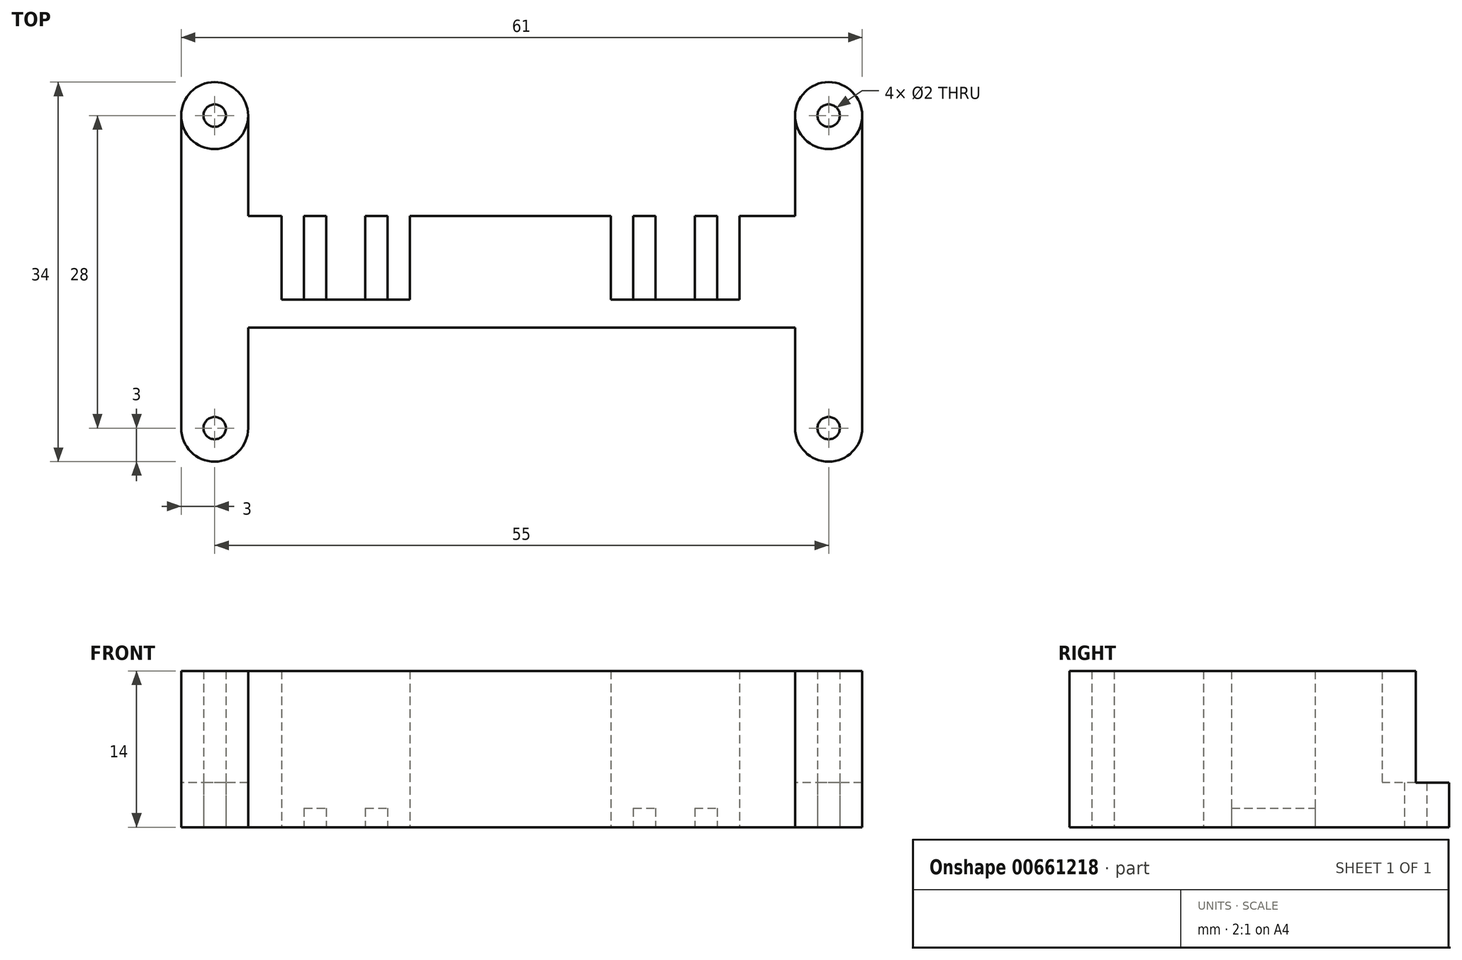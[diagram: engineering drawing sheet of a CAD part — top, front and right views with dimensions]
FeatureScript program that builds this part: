
annotation { "Feature Type Name" : "Feature", "Feature Type Description" : "" }
export const myFeature = defineFeature(function(context is Context, id is Id, definition is map)
    precondition{}
    {
        {
            var Q0;
            Q0=qCreatedBy(makeId("Top.planeOp"),FACE);
            var sketch = newSketch(context, id + "F0", { "sketchPlane" : qUnion([Q0])});
            skLineSegment(sketch, "E0", {"start": v(55, 0) * mm, "end": v(55, -9) * mm});
            skLineSegment(sketch, "E1", {"start": v(61, -9) * mm, "end": v(61, 19) * mm});
            skLineSegment(sketch, "E2", {"start": v(55, 19) * mm, "end": v(55, 10) * mm});
            skLineSegment(sketch, "E3", {"start": v(55, 10) * mm, "end": v(50, 10) * mm});
            skLineSegment(sketch, "E4", {"start": v(50, 10) * mm, "end": v(50, 2.5) * mm});
            skLineSegment(sketch, "E5", {"start": v(50, 2.5) * mm, "end": v(38.5, 2.5) * mm});
            skLineSegment(sketch, "E6", {"start": v(38.5, 2.5) * mm, "end": v(38.5, 10) * mm});
            skLineSegment(sketch, "E7", {"start": v(38.5, 10) * mm, "end": v(20.5, 10) * mm});
            skLineSegment(sketch, "E8", {"start": v(20.5, 10) * mm, "end": v(20.5, 2.5) * mm});
            skLineSegment(sketch, "E9", {"start": v(20.5, 2.5) * mm, "end": v(9, 2.5) * mm});
            skLineSegment(sketch, "E10", {"start": v(9, 2.5) * mm, "end": v(9, 10) * mm});
            skLineSegment(sketch, "E11", {"start": v(9, 10) * mm, "end": v(6, 10) * mm});
            skLineSegment(sketch, "E12", {"start": v(6, 10) * mm, "end": v(6, 19) * mm});
            skLineSegment(sketch, "E13", {"start": v(0, 19) * mm, "end": v(0, -9) * mm});
            skLineSegment(sketch, "E14", {"start": v(6, -9) * mm, "end": v(6, 0) * mm});
            skArc(sketch, "E15", {"start": v(0, 19) * mm, "mid": v(3, 22) * mm, "end": v(6, 19) * mm});
            skArc(sketch, "E16", {"start": v(6, -9) * mm, "mid": v(3, -12) * mm, "end": v(0, -9) * mm});
            skArc(sketch, "E17", {"start": v(61, -9) * mm, "mid": v(58, -12) * mm, "end": v(55, -9) * mm});
            skArc(sketch, "E18", {"start": v(55, 19) * mm, "mid": v(58, 22) * mm, "end": v(61, 19) * mm});
            skLineSegment(sketch, "E19", {"start": v(6, 0) * mm, "end": v(55, 0) * mm});
            skSolve(sketch);
        }
        {
            var Q0;
            Q0=makeQuery(id+"F0.imprint","IMPRINT",FACE,{"disambiguationData":[TD([[makeQuery(id+"F0.imprint","IMPRINT",EDGE,{"derivedFrom":sQuery(id+"F0.wireOp",EDGE,"E0")}),1.0]])]});
            extrude(context, id + "F1", {"entities" : qUnion([Q0]), "depth" : 4 * mm, "offsetDistance" : 25 * mm});
        }
        {
            var Q0;
            Q0=qCreatedBy(makeId("Top.planeOp"),FACE);
            var sketch = newSketch(context, id + "F2", { "sketchPlane" : qUnion([Q0])});
            skLineSegment(sketch, "E20.bottom", {"start": v(11, 2.5) * mm, "end": v(13, 2.5) * mm});
            skLineSegment(sketch, "E20.top", {"start": v(11, 10) * mm, "end": v(13, 10) * mm});
            skLineSegment(sketch, "E20.left", {"start": v(11, 2.5) * mm, "end": v(11, 10) * mm});
            skLineSegment(sketch, "E20.right", {"start": v(13, 2.5) * mm, "end": v(13, 10) * mm});
            skLineSegment(sketch, "E21.bottom", {"start": v(16.5, 2.5) * mm, "end": v(18.5, 2.5) * mm});
            skLineSegment(sketch, "E21.top", {"start": v(16.5, 10) * mm, "end": v(18.5, 10) * mm});
            skLineSegment(sketch, "E21.left", {"start": v(16.5, 2.5) * mm, "end": v(16.5, 10) * mm});
            skLineSegment(sketch, "E21.right", {"start": v(18.5, 2.5) * mm, "end": v(18.5, 10) * mm});
            skLineSegment(sketch, "E22.bottom", {"start": v(40.5, 2.5) * mm, "end": v(42.5, 2.5) * mm});
            skLineSegment(sketch, "E22.top", {"start": v(40.5, 10) * mm, "end": v(42.5, 10) * mm});
            skLineSegment(sketch, "E22.left", {"start": v(40.5, 2.5) * mm, "end": v(40.5, 10) * mm});
            skLineSegment(sketch, "E22.right", {"start": v(42.5, 2.5) * mm, "end": v(42.5, 10) * mm});
            skLineSegment(sketch, "E23.bottom", {"start": v(46, 2.5) * mm, "end": v(48, 2.5) * mm});
            skLineSegment(sketch, "E23.top", {"start": v(46, 10) * mm, "end": v(48, 10) * mm});
            skLineSegment(sketch, "E23.left", {"start": v(46, 2.5) * mm, "end": v(46, 10) * mm});
            skLineSegment(sketch, "E23.right", {"start": v(48, 2.5) * mm, "end": v(48, 10) * mm});
            skSolve(sketch);
        }
        {
            var Q0;
            Q0=makeQuery(id+"F2.imprint","IMPRINT",FACE,{"disambiguationData":[TD([[makeQuery(id+"F2.imprint","IMPRINT",EDGE,{"derivedFrom":sQuery(id+"F2.wireOp",EDGE,"E20.bottom")}),1.0]])]});
            var Q1;
            Q1=makeQuery(id+"F2.imprint","IMPRINT",FACE,{"disambiguationData":[TD([[makeQuery(id+"F2.imprint","IMPRINT",EDGE,{"derivedFrom":sQuery(id+"F2.wireOp",EDGE,"E21.bottom")}),1.0]])]});
            var Q2;
            Q2=makeQuery(id+"F2.imprint","IMPRINT",FACE,{"disambiguationData":[TD([[makeQuery(id+"F2.imprint","IMPRINT",EDGE,{"derivedFrom":sQuery(id+"F2.wireOp",EDGE,"E22.bottom")}),1.0]])]});
            var Q3;
            Q3=makeQuery(id+"F2.imprint","IMPRINT",FACE,{"disambiguationData":[TD([[makeQuery(id+"F2.imprint","IMPRINT",EDGE,{"derivedFrom":sQuery(id+"F2.wireOp",EDGE,"E23.bottom")}),1.0]])]});
            extrude(context, id + "F3", {"entities" : qUnion([Q0, Q1, Q2, Q3]), "operationType" : NewBodyOperationType.ADD, "depth" : 1.7 * mm, "offsetDistance" : 25 * mm});
        }
        {
            var Q0;
            Q0=makeQuery(id+"F1.opExtrude","CAP_FACE",FACE,{"disambiguationData":[OSD([sQuery(id+"F0.wireOp",EDGE,"E0"),sQuery(id+"F0.wireOp",EDGE,"E1"),sQuery(id+"F0.wireOp",EDGE,"E2"),sQuery(id+"F0.wireOp",EDGE,"E3"),sQuery(id+"F0.wireOp",EDGE,"E4"),sQuery(id+"F0.wireOp",EDGE,"E5"),sQuery(id+"F0.wireOp",EDGE,"E6"),sQuery(id+"F0.wireOp",EDGE,"E7"),sQuery(id+"F0.wireOp",EDGE,"E8"),sQuery(id+"F0.wireOp",EDGE,"E9"),sQuery(id+"F0.wireOp",EDGE,"E10"),sQuery(id+"F0.wireOp",EDGE,"E11"),sQuery(id+"F0.wireOp",EDGE,"E12"),sQuery(id+"F0.wireOp",EDGE,"E13"),sQuery(id+"F0.wireOp",EDGE,"E14"),sQuery(id+"F0.wireOp",EDGE,"E15"),sQuery(id+"F0.wireOp",EDGE,"E16"),sQuery(id+"F0.wireOp",EDGE,"E17"),sQuery(id+"F0.wireOp",EDGE,"E18"),sQuery(id+"F0.wireOp",EDGE,"E19")])],"isStart":false});
            var sketch = newSketch(context, id + "F4", { "sketchPlane" : qUnion([Q0])});
            skCircle(sketch, "E24", {"center": v(3, 19) * mm, "radius": 3 * mm});
            skCircle(sketch, "E25", {"center": v(58, 19) * mm, "radius": 3 * mm});
            skCircle(sketch, "E26", {"center": v(58, -9) * mm, "radius": 3 * mm});
            skCircle(sketch, "E27", {"center": v(3, -9) * mm, "radius": 3 * mm});
            skSolve(sketch);
        }
        {
            var Q0;
            {var subQ0=sQuery(id+"F4.wireOp",EDGE,"E24");Q0=makeQuery(id+"F4.imprint","IMPRINT",FACE,{"disambiguationData":[TD([[makeQuery(id+"F4.imprint","IMPRINT",EDGE,{"disambiguationData":[OD(0.0)],"derivedFrom":subQ0}),-1.0]])]});}
            var Q1;
            {var subQ0=sQuery(id+"F4.wireOp",EDGE,"E27");Q1=makeQuery(id+"F4.imprint","IMPRINT",FACE,{"disambiguationData":[TD([[makeQuery(id+"F4.imprint","IMPRINT",EDGE,{"disambiguationData":[OD(0.0)],"derivedFrom":subQ0}),1.0]])]});}
            var Q2;
            {var subQ0=sQuery(id+"F4.wireOp",EDGE,"E25");Q2=makeQuery(id+"F4.imprint","IMPRINT",FACE,{"disambiguationData":[TD([[makeQuery(id+"F4.imprint","IMPRINT",EDGE,{"disambiguationData":[OD(0.0)],"derivedFrom":subQ0}),-1.0]])]});}
            var Q3;
            {var subQ0=sQuery(id+"F4.wireOp",EDGE,"E26");Q3=makeQuery(id+"F4.imprint","IMPRINT",FACE,{"disambiguationData":[TD([[makeQuery(id+"F4.imprint","IMPRINT",EDGE,{"disambiguationData":[OD(0.0)],"derivedFrom":subQ0}),1.0]])]});}
            extrude(context, id + "F5", {"entities" : qUnion([Q0, Q1, Q2, Q3]), "operationType" : NewBodyOperationType.ADD, "depth" : 10 * mm, "offsetDistance" : 25 * mm});
        }
        {
            var Q0;
            Q0=makeQuery(id+"F3.boolean.opBoolean","MERGE",FACE,{"derivedFrom":[makeQuery(id+"F1.opExtrude","CAP_FACE",FACE,{"disambiguationData":[OSD([sQuery(id+"F0.wireOp",EDGE,"E0"),sQuery(id+"F0.wireOp",EDGE,"E1"),sQuery(id+"F0.wireOp",EDGE,"E2"),sQuery(id+"F0.wireOp",EDGE,"E3"),sQuery(id+"F0.wireOp",EDGE,"E4"),sQuery(id+"F0.wireOp",EDGE,"E5"),sQuery(id+"F0.wireOp",EDGE,"E6"),sQuery(id+"F0.wireOp",EDGE,"E7"),sQuery(id+"F0.wireOp",EDGE,"E8"),sQuery(id+"F0.wireOp",EDGE,"E9"),sQuery(id+"F0.wireOp",EDGE,"E10"),sQuery(id+"F0.wireOp",EDGE,"E11"),sQuery(id+"F0.wireOp",EDGE,"E12"),sQuery(id+"F0.wireOp",EDGE,"E13"),sQuery(id+"F0.wireOp",EDGE,"E14"),sQuery(id+"F0.wireOp",EDGE,"E15"),sQuery(id+"F0.wireOp",EDGE,"E16"),sQuery(id+"F0.wireOp",EDGE,"E17"),sQuery(id+"F0.wireOp",EDGE,"E18"),sQuery(id+"F0.wireOp",EDGE,"E19")])],"isStart":true}),makeQuery(id+"F3.opExtrude","CAP_FACE",FACE,{"disambiguationData":[OSD([sQuery(id+"F2.wireOp",EDGE,"E20.bottom"),sQuery(id+"F2.wireOp",EDGE,"E20.top"),sQuery(id+"F2.wireOp",EDGE,"E20.left"),sQuery(id+"F2.wireOp",EDGE,"E20.right")])],"isStart":true}),makeQuery(id+"F3.opExtrude","CAP_FACE",FACE,{"disambiguationData":[OSD([sQuery(id+"F2.wireOp",EDGE,"E21.bottom"),sQuery(id+"F2.wireOp",EDGE,"E21.top"),sQuery(id+"F2.wireOp",EDGE,"E21.left"),sQuery(id+"F2.wireOp",EDGE,"E21.right")])],"isStart":true}),makeQuery(id+"F3.opExtrude","CAP_FACE",FACE,{"disambiguationData":[OSD([sQuery(id+"F2.wireOp",EDGE,"E22.bottom"),sQuery(id+"F2.wireOp",EDGE,"E22.top"),sQuery(id+"F2.wireOp",EDGE,"E22.left"),sQuery(id+"F2.wireOp",EDGE,"E22.right")])],"isStart":true}),makeQuery(id+"F3.opExtrude","CAP_FACE",FACE,{"disambiguationData":[OSD([sQuery(id+"F2.wireOp",EDGE,"E23.bottom"),sQuery(id+"F2.wireOp",EDGE,"E23.top"),sQuery(id+"F2.wireOp",EDGE,"E23.left"),sQuery(id+"F2.wireOp",EDGE,"E23.right")])],"isStart":true})]});
            var sketch = newSketch(context, id + "F6", { "sketchPlane" : qUnion([Q0])});
            skCircle(sketch, "E28", {"center": v(3, 9) * mm, "radius": 1 * mm});
            skCircle(sketch, "E29", {"center": v(58, 9) * mm, "radius": 1 * mm});
            skCircle(sketch, "E30", {"center": v(58, -19) * mm, "radius": 1 * mm});
            skCircle(sketch, "E31", {"center": v(3, -19) * mm, "radius": 1 * mm});
            skSolve(sketch);
        }
        {
            var Q0;
            Q0=qSketchRegion(id+"F6",true);
            extrude(context, id + "F7", {"entities" : qUnion([Q0]), "operationType" : NewBodyOperationType.REMOVE, "oppositeDirection" : true, "depth" : 25 * mm, "offsetDistance" : 25 * mm});
        }
    });
